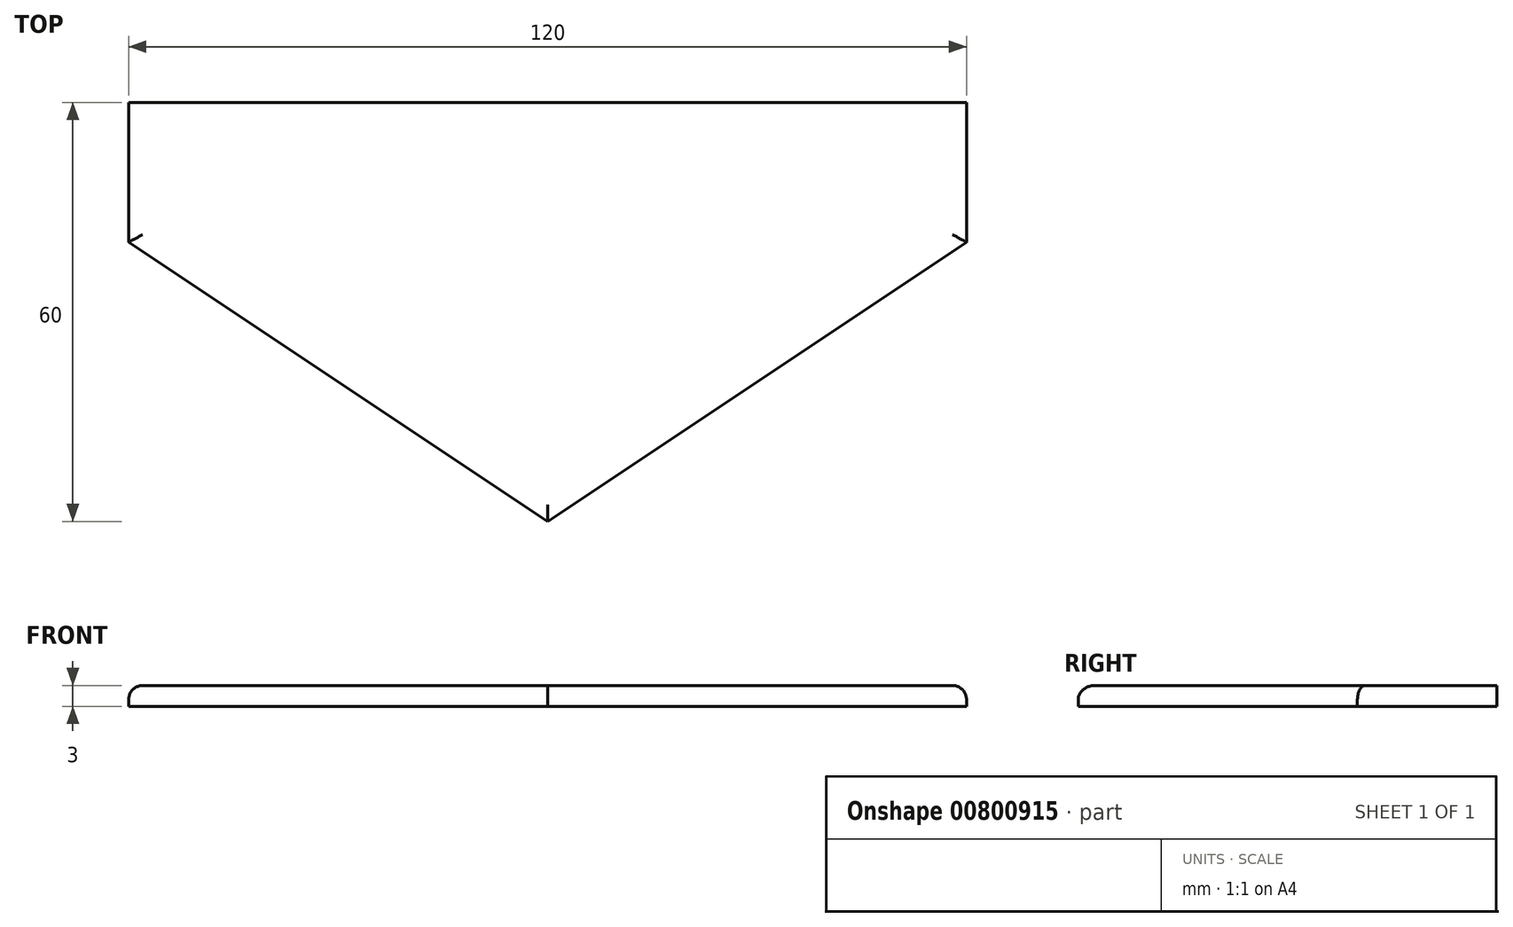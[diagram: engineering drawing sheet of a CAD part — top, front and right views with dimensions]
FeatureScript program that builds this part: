
annotation { "Feature Type Name" : "Feature", "Feature Type Description" : "" }
export const myFeature = defineFeature(function(context is Context, id is Id, definition is map)
    precondition{}
    {
        {
            var Q0;
            Q0=qCreatedBy(makeId("Top.planeOp"),FACE);
            var sketch = newSketch(context, id + "F0", { "sketchPlane" : qUnion([Q0])});
            skLineSegment(sketch, "E0", {"start": v(-60, 30) * mm, "end": v(60, 30) * mm});
            skLineSegment(sketch, "E1", {"start": v(60, 30) * mm, "end": v(60, 10) * mm});
            skLineSegment(sketch, "E2", {"start": v(60, 10) * mm, "end": v(0, -30) * mm});
            skLineSegment(sketch, "E3", {"start": v(0, -30) * mm, "end": v(-60, 10) * mm});
            skLineSegment(sketch, "E4", {"start": v(-60, 10) * mm, "end": v(-60, 30) * mm});
            skLineSegment(sketch, "E5", {"start": v(0, -30) * mm, "end": v(0, 30) * mm});
            skSolve(sketch);
        }
        {
            var Q0;
            Q0=makeQuery(id+"F0.imprint","IMPRINT",FACE,{"disambiguationData":[TD([[makeQuery(id+"F0.imprint","IMPRINT",EDGE,{"derivedFrom":sQuery(id+"F0.wireOp",EDGE,"E3")}),-1.0]])]});
            var Q1;
            {var subQ0=sQuery(id+"F0.wireOp",EDGE,"E1");Q1=makeQuery(id+"F0.imprint","IMPRINT",FACE,{"disambiguationData":[TD([[makeQuery(id+"F0.imprint","IMPRINT",EDGE,{"derivedFrom":subQ0}),-1.0]])]});}
            extrude(context, id + "F1", {"entities" : qUnion([Q0, Q1]), "endBound" : BoundingType.SYMMETRIC, "depth" : 3 * mm, "offsetDistance" : 25 * mm});
        }
        {
            var Q0;
            Q0=makeQuery(id+"F1.opExtrude","CAP_EDGE",EDGE,{"disambiguationData":[OSD([sQuery(id+"F0.wireOp",EDGE,"E2")])],"isStart":false});
            var Q1;
            Q1=makeQuery(id+"F1.opExtrude","CAP_EDGE",EDGE,{"disambiguationData":[OSD([sQuery(id+"F0.wireOp",EDGE,"E3")])],"isStart":false});
            var Q2;
            Q2=makeQuery(id+"F1.opExtrude","CAP_EDGE",EDGE,{"disambiguationData":[OSD([sQuery(id+"F0.wireOp",EDGE,"E4")])],"isStart":false});
            var Q3;
            Q3=makeQuery(id+"F1.opExtrude","CAP_EDGE",EDGE,{"disambiguationData":[OSD([sQuery(id+"F0.wireOp",EDGE,"E1")])],"isStart":false});
            fillet(context, id + "F2", {"entities" : qUnion([Q0, Q1, Q2, Q3]), "radius" : 2 * mm, "tangentPropagation" : true, "allowEdgeOverflow" : false});
        }
    });
